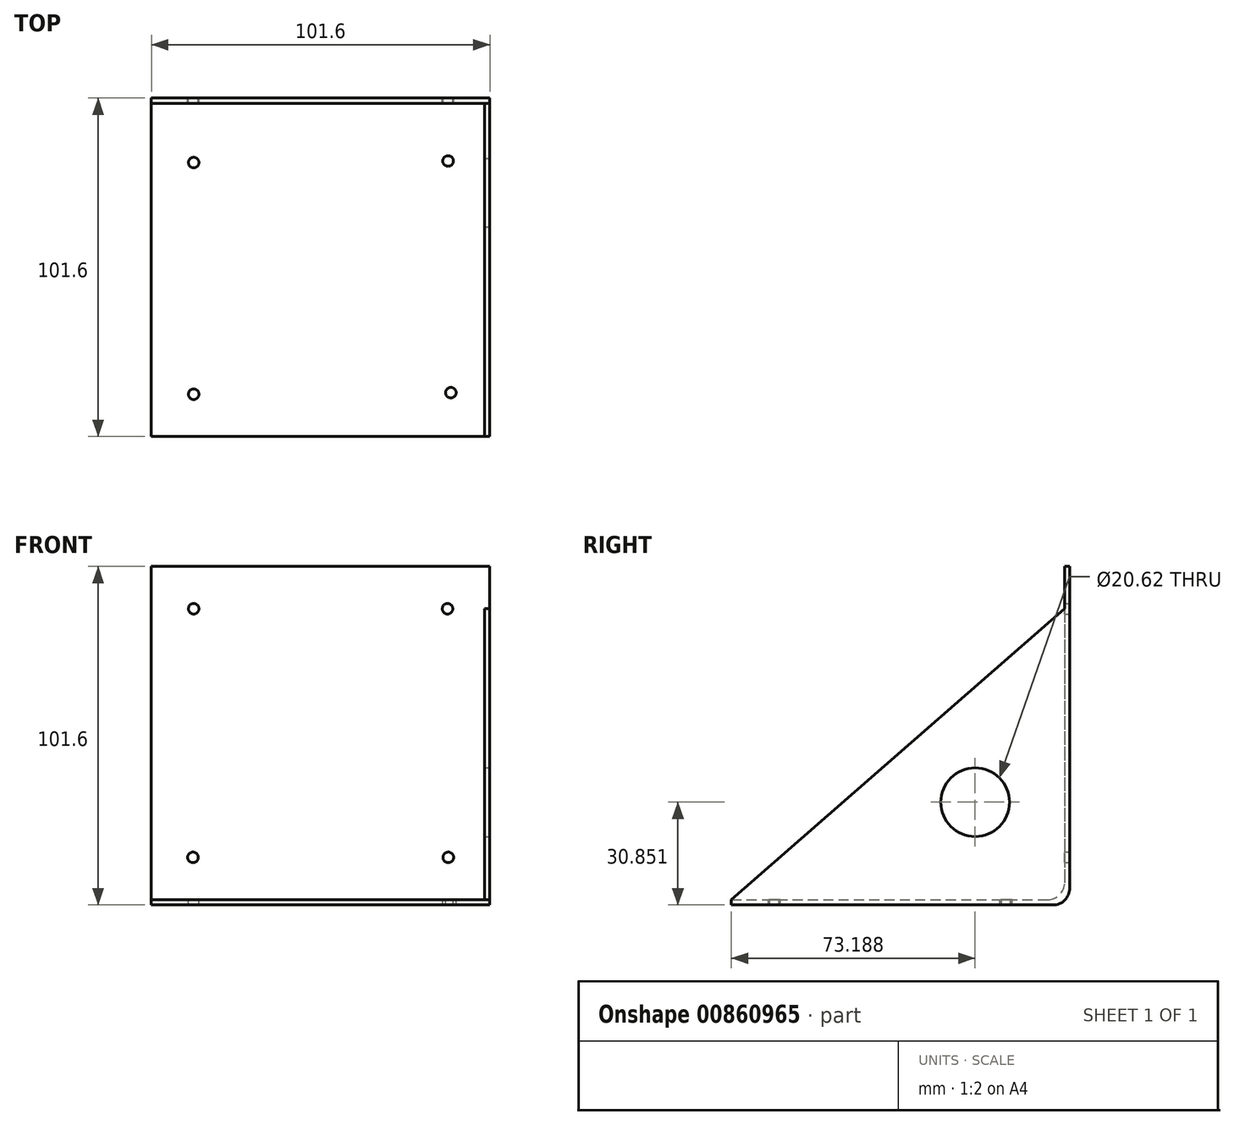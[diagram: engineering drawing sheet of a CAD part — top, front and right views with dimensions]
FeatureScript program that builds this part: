
annotation { "Feature Type Name" : "Feature", "Feature Type Description" : "" }
export const myFeature = defineFeature(function(context is Context, id is Id, definition is map)
    precondition{}
    {
        {
            var Q0;
            Q0=qCreatedBy(makeId("Front.planeOp"),FACE);
            var sketch = newSketch(context, id + "F0", { "sketchPlane" : qUnion([Q0])});
            skLineSegment(sketch, "E0.bottom", {"start": v(-51.38, 55.3) * mm, "end": v(50.22, 55.3) * mm});
            skLineSegment(sketch, "E0.top", {"start": v(-51.38, -46.3) * mm, "end": v(50.22, -46.3) * mm});
            skLineSegment(sketch, "E0.left", {"start": v(-51.38, 55.3) * mm, "end": v(-51.38, -46.3) * mm});
            skLineSegment(sketch, "E0.right", {"start": v(50.22, 55.3) * mm, "end": v(50.22, -46.3) * mm});
            skLineSegment(sketch, "E1", {"start": v(-51.38, -46.3) * mm, "end": v(-51.38, -44.71) * mm});
            skLineSegment(sketch, "E2", {"start": v(-51.38, -44.71) * mm, "end": v(50.22, -44.71) * mm});
            skLineSegment(sketch, "E3.bottom", {"start": v(-51.38, 55.3) * mm, "end": v(-38.68, 55.3) * mm});
            skLineSegment(sketch, "E3.top", {"start": v(-51.38, 42.6) * mm, "end": v(-38.68, 42.6) * mm});
            skLineSegment(sketch, "E3.left", {"start": v(-51.38, 55.3) * mm, "end": v(-51.38, 42.6) * mm});
            skLineSegment(sketch, "E3.right", {"start": v(-38.68, 55.3) * mm, "end": v(-38.68, 42.6) * mm});
            skCircle(sketch, "E4", {"center": v(-38.68, 42.6) * mm, "radius": 1.59 * mm});
            skLineSegment(sketch, "E5", {"start": v(-38.68, -44.71) * mm, "end": v(-38.91, -32.01) * mm});
            skCircle(sketch, "E6", {"center": v(-38.91, -32.01) * mm, "radius": 1.59 * mm});
            skLineSegment(sketch, "E7", {"start": v(-0.58, 55.3) * mm, "end": v(-0.58, -44.71) * mm});
            skCircle(sketch, "E8.MirrorC", {"center": v(37.52, 42.6) * mm, "radius": 1.59 * mm});
            skCircle(sketch, "E9.MirrorC", {"center": v(37.75, -32.01) * mm, "radius": 1.59 * mm});
            skSolve(sketch);
        }
        {
            var Q0;
            {var subQ0=sQuery(id+"F0.wireOp",EDGE,"E0.top");Q0=makeQuery(id+"F0.imprint","IMPRINT",FACE,{"disambiguationData":[TD([[makeQuery(id+"F0.imprint","IMPRINT",EDGE,{"derivedFrom":subQ0}),1.0]])]});}
            extrude(context, id + "F1", {"entities" : qUnion([Q0]), "depth" : 101.6 * mm, "offsetDistance" : 25.4 * mm});
        }
        {
            var Q0;
            Q0 = qSketchRegion(id + "F0", true);
            extrude(context, id + "F2", {"entities" : qUnion([Q0]), "operationType" : NewBodyOperationType.ADD, "depth" : 1.59 * mm, "offsetDistance" : 25.4 * mm});
        }
        {
            var Q0;
            {var subQ0=sQuery(id+"F0.wireOp",EDGE,"E0.right");Q0=makeQuery(id+"F2.boolean.opBoolean","MERGE",FACE,{"derivedFrom":[makeQuery(id+"F1.opExtrude","SWEPT_FACE",FACE,{"disambiguationData":[OSD([subQ0])]}),makeQuery(id+"F2.opExtrude","SWEPT_FACE",FACE,{"disambiguationData":[OSD([subQ0])]})]});}
            var sketch = newSketch(context, id + "F3", { "sketchPlane" : qUnion([Q0])});
            skLineSegment(sketch, "E10", {"start": v(-1.59, 55.3) * mm, "end": v(-1.59, 42.6) * mm});
            skLineSegment(sketch, "E11", {"start": v(-1.59, 42.6) * mm, "end": v(-101.6, -44.71) * mm});
            skSolve(sketch);
        }
        {
            var Q0;
            Q0 = qSketchRegion(id + "F3", true);
            var Q1;
            {var subQ0=sQuery(id+"F3.wireOp",EDGE,"E11");Q1=makeQuery(id+"F3.imprint","IMPRINT",FACE,{"disambiguationData":[TD([[makeQuery(id+"F3.imprint","IMPRINT",EDGE,{"derivedFrom":subQ0}),1.0]])]});}
            extrude(context, id + "F4", {"entities" : qUnion([Q0, Q1]), "oppositeDirection" : true, "depth" : 1.59 * mm, "offsetDistance" : 25.4 * mm});
        }
        {
            var Q0;
            Q0=makeQuery(id+"F1.opExtrude","CAP_EDGE",EDGE,{"disambiguationData":[OSD([sQuery(id+"F0.wireOp",EDGE,"E0.top")])],"isStart":true});
            fillet(context, id + "F5", {"entities" : qUnion([Q0]), "radius" : 5.08 * mm, "tangentPropagation" : true, "allowEdgeOverflow" : false});
        }
        {
            var Q0;
            Q0=makeQuery(id+"F2.boolean.opBoolean","INTERSECT",EDGE,{"derivedFrom":[makeQuery(id+"F1.opExtrude","SWEPT_FACE",FACE,{"disambiguationData":[OSD([sQuery(id+"F0.wireOp",EDGE,"E2")])]}),makeQuery(id+"F2.opExtrude","CAP_FACE",FACE,{"disambiguationData":[OSD([sQuery(id+"F0.wireOp",EDGE,"E0.bottom"),sQuery(id+"F0.wireOp",EDGE,"E0.top"),sQuery(id+"F0.wireOp",EDGE,"E0.left"),sQuery(id+"F0.wireOp",EDGE,"E0.right"),sQuery(id+"F0.wireOp",EDGE,"E1"),sQuery(id+"F0.wireOp",EDGE,"E3.bottom"),sQuery(id+"F0.wireOp",EDGE,"E3.left"),sQuery(id+"F0.wireOp",EDGE,"E4"),sQuery(id+"F0.wireOp",EDGE,"E6"),sQuery(id+"F0.wireOp",EDGE,"E8.MirrorC"),sQuery(id+"F0.wireOp",EDGE,"E9.MirrorC")])],"isStart":false})]});
            fillet(context, id + "F6", {"entities" : qUnion([Q0]), "radius" : 5.08 * mm, "tangentPropagation" : true, "allowEdgeOverflow" : false});
        }
        {
            var Q0;
            Q0=makeQuery(id+"F1.opExtrude","SWEPT_FACE",FACE,{"disambiguationData":[OSD([sQuery(id+"F0.wireOp",EDGE,"E2")])]});
            var sketch = newSketch(context, id + "F7", { "sketchPlane" : qUnion([Q0])});
            skLineSegment(sketch, "E12", {"start": v(-51.38, -6.67) * mm, "end": v(-38.68, -6.67) * mm});
            skLineSegment(sketch, "E13", {"start": v(-38.68, -6.67) * mm, "end": v(-38.68, -19.37) * mm});
            skCircle(sketch, "E14", {"center": v(-38.68, -19.37) * mm, "radius": 1.59 * mm});
            skLineSegment(sketch, "E15", {"start": v(-0.58, -6.67) * mm, "end": v(0, -101.6) * mm});
            skLineSegment(sketch, "E16", {"start": v(-51.38, -54.13) * mm, "end": v(50.22, -54.13) * mm});
            skCircle(sketch, "E17.MirrorC", {"center": v(-38.68, -88.9) * mm, "radius": 1.59 * mm});
            skCircle(sketch, "E18.MirrorC", {"center": v(37.67, -18.9) * mm, "radius": 1.59 * mm});
            skCircle(sketch, "E19.MirrorC", {"center": v(38.52, -88.43) * mm, "radius": 1.59 * mm});
            skSolve(sketch);
        }
        {
            var Q0;
            Q0 = qSketchRegion(id + "F7", true);
            extrude(context, id + "F8", {"entities" : qUnion([Q0]), "operationType" : NewBodyOperationType.REMOVE, "oppositeDirection" : true, "depth" : 25.4 * mm, "offsetDistance" : 25.4 * mm});
        }
        {
            var Q0;
            Q0=makeQuery(id+"F4.opExtrude","SWEPT_BODY",BODY,{"disambiguationData":[OSD([sQuery(id+"F0.wireOp",EDGE,"E0.right"),sQuery(id+"F0.wireOp",EDGE,"E2"),sQuery(id+"F3.wireOp",EDGE,"E11")])]});
            var Q1;
            Q1=makeQuery(id+"F1.opExtrude","SWEPT_BODY",BODY,{"disambiguationData":[OSD([sQuery(id+"F0.wireOp",EDGE,"E0.top"),sQuery(id+"F0.wireOp",EDGE,"E0.right"),sQuery(id+"F0.wireOp",EDGE,"E1"),sQuery(id+"F0.wireOp",EDGE,"E2")])]});
            booleanBodies(context, id + "F9", {"operationType" : BooleanOperationType.UNION, "tools" : qUnion([Q0, Q1])});
        }
        {
            var Q0;
            {var subQ0=sQuery(id+"F0.wireOp",EDGE,"E0.right");Q0=makeQuery(id+"F9.opBoolean","MERGE",FACE,{"derivedFrom":[makeQuery(id+"F4.opExtrude","CAP_FACE",FACE,{"disambiguationData":[OSD([subQ0,sQuery(id+"F0.wireOp",EDGE,"E2"),sQuery(id+"F3.wireOp",EDGE,"E11")])],"isStart":true}),makeQuery(id+"F2.boolean.opBoolean","MERGE",FACE,{"derivedFrom":[makeQuery(id+"F1.opExtrude","SWEPT_FACE",FACE,{"disambiguationData":[OSD([subQ0])]}),makeQuery(id+"F2.opExtrude","SWEPT_FACE",FACE,{"disambiguationData":[OSD([subQ0])]})]})]});}
            var sketch = newSketch(context, id + "F10", { "sketchPlane" : qUnion([Q0])});
            skCircle(sketch, "E20", {"center": v(-28.41, -15.45) * mm, "radius": 10.31 * mm});
            skSolve(sketch);
        }
        {
            var Q0;
            Q0=makeQuery(id+"F10.imprint","IMPRINT",FACE,{"disambiguationData":[TD([[makeQuery(id+"F10.imprint","IMPRINT",EDGE,{"derivedFrom":sQuery(id+"F10.wireOp",EDGE,"E20")}),1.0]])]});
            extrude(context, id + "F11", {"entities" : qUnion([Q0]), "operationType" : NewBodyOperationType.REMOVE, "oppositeDirection" : true, "depth" : 25.4 * mm, "offsetDistance" : 25.4 * mm});
        }
    });
